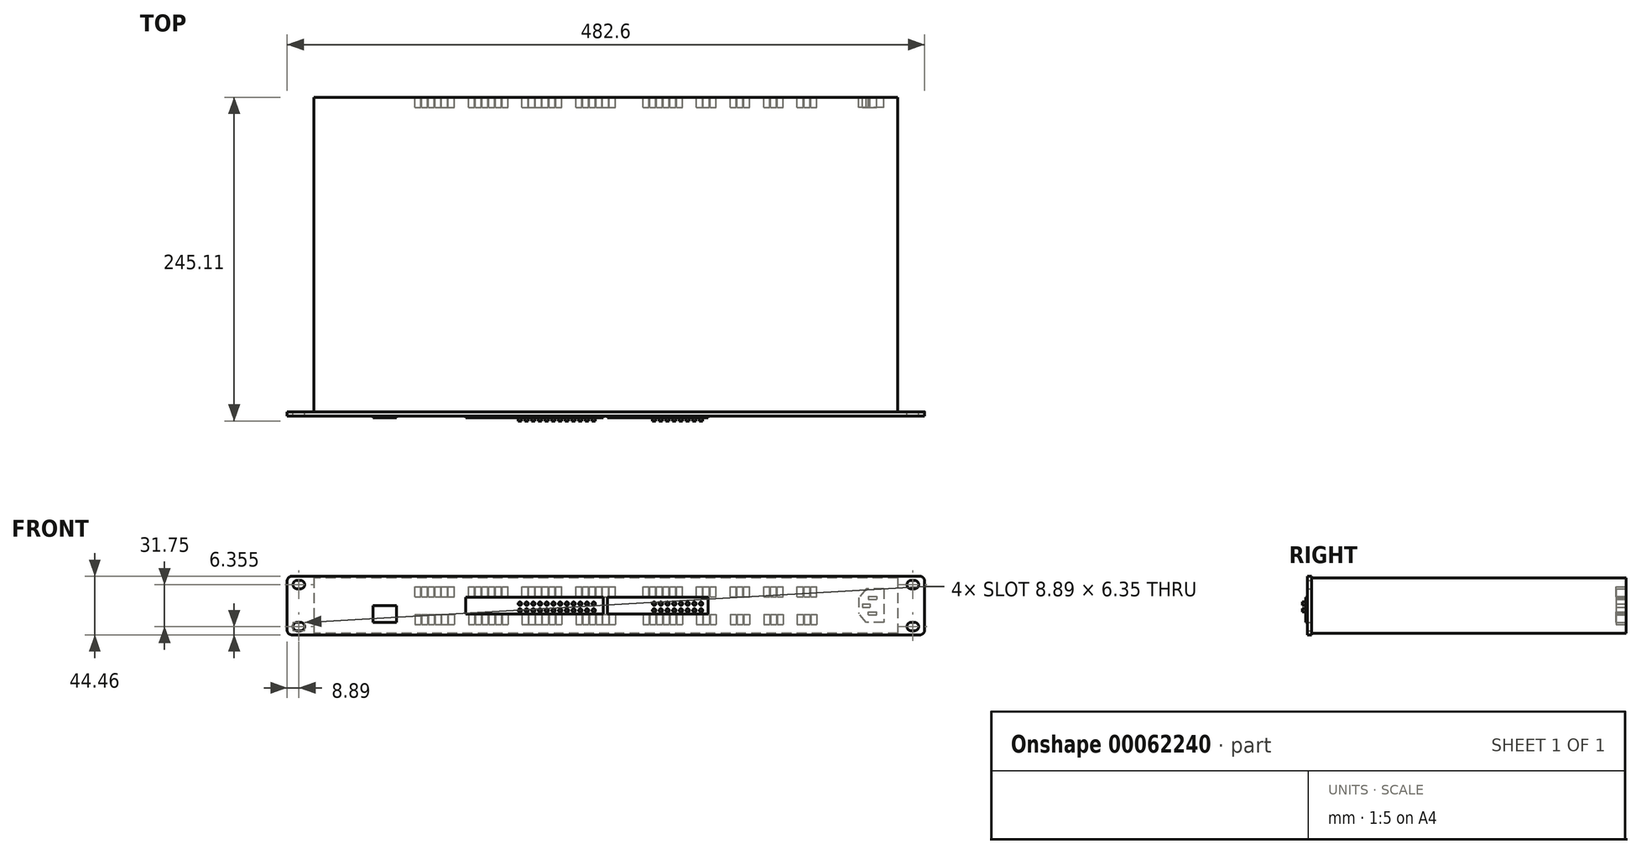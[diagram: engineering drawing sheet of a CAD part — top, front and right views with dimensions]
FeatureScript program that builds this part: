
annotation { "Feature Type Name" : "Feature", "Feature Type Description" : "" }
export const myFeature = defineFeature(function(context is Context, id is Id, definition is map)
    precondition{}
    {
        {
            var Q0;
            Q0=qCreatedBy(makeId("Front.planeOp"),FACE);
            var sketch = newSketch(context, id + "F0", { "sketchPlane" : qUnion([Q0])});
            skLineSegment(sketch, "E0.bottom", {"start": v(-237.5, 22.23) * mm, "end": v(237.5, 22.23) * mm});
            skLineSegment(sketch, "E0.top", {"start": v(-237.5, -22.22) * mm, "end": v(237.5, -22.22) * mm});
            skLineSegment(sketch, "E0.left", {"start": v(-241.3, 18.42) * mm, "end": v(-241.3, -18.41) * mm});
            skLineSegment(sketch, "E0.right", {"start": v(241.3, 18.42) * mm, "end": v(241.3, -18.42) * mm});
            skPoint(sketch, "E0.middle", {"position": v(0, 0) * mm});
            skArc(sketch, "E1", {"start": v(-233.68, 19.05) * mm, "mid": v(-236.86, 15.88) * mm, "end": v(-233.68, 12.7) * mm});
            skArc(sketch, "E2", {"start": v(-231.14, 12.7) * mm, "mid": v(-227.97, 15.88) * mm, "end": v(-231.14, 19.05) * mm});
            skLineSegment(sketch, "E3", {"start": v(-233.68, 12.7) * mm, "end": v(-231.14, 12.7) * mm});
            skLineSegment(sketch, "E4", {"start": v(-233.68, 19.05) * mm, "end": v(-231.14, 19.05) * mm});
            skPoint(sketch, "E5.visualSharp", {"position": v(-241.3, 22.23) * mm});
            skArc(sketch, "E5.filletArc", {"start": v(-237.5, 22.23) * mm, "mid": v(-240.18, 21.1) * mm, "end": v(-241.3, 18.42) * mm});
            skPoint(sketch, "E6.visualSharp", {"position": v(-241.3, -22.22) * mm});
            skArc(sketch, "E6.filletArc", {"start": v(-241.3, -18.41) * mm, "mid": v(-240.18, -21.1) * mm, "end": v(-237.5, -22.22) * mm});
            skPoint(sketch, "E7.visualSharp", {"position": v(241.3, 22.23) * mm});
            skArc(sketch, "E7.filletArc", {"start": v(241.3, 18.42) * mm, "mid": v(240.18, 21.1) * mm, "end": v(237.5, 22.23) * mm});
            skPoint(sketch, "E8.visualSharp", {"position": v(241.3, -22.22) * mm});
            skArc(sketch, "E8.filletArc", {"start": v(237.5, -22.23) * mm, "mid": v(240.18, -21.1) * mm, "end": v(241.3, -18.42) * mm});
            skLineSegment(sketch, "E9.MirrorCS", {"start": v(-233.68, -19.05) * mm, "end": v(-231.14, -19.05) * mm});
            skArc(sketch, "E10.MirrorCS", {"start": v(-231.14, -12.7) * mm, "mid": v(-227.97, -15.88) * mm, "end": v(-231.14, -19.05) * mm});
            skLineSegment(sketch, "E11.MirrorCS", {"start": v(-233.68, -12.7) * mm, "end": v(-231.14, -12.7) * mm});
            skArc(sketch, "E12.MirrorCS", {"start": v(-233.68, -19.05) * mm, "mid": v(-236.86, -15.88) * mm, "end": v(-233.68, -12.7) * mm});
            skLineSegment(sketch, "E13.MirrorCS", {"start": v(233.68, 12.7) * mm, "end": v(231.14, 12.7) * mm});
            skLineSegment(sketch, "E14.MirrorCS", {"start": v(233.68, -12.7) * mm, "end": v(231.14, -12.7) * mm});
            skLineSegment(sketch, "E15.MirrorCS", {"start": v(233.68, 19.05) * mm, "end": v(231.14, 19.05) * mm});
            skLineSegment(sketch, "E16.MirrorCS", {"start": v(233.68, -19.05) * mm, "end": v(231.14, -19.05) * mm});
            skArc(sketch, "E17.MirrorCS", {"start": v(233.68, -19.05) * mm, "mid": v(236.86, -15.88) * mm, "end": v(233.68, -12.7) * mm});
            skArc(sketch, "E18.MirrorCS", {"start": v(231.14, 12.7) * mm, "mid": v(227.97, 15.88) * mm, "end": v(231.14, 19.05) * mm});
            skArc(sketch, "E19.MirrorCS", {"start": v(233.68, 19.05) * mm, "mid": v(236.86, 15.88) * mm, "end": v(233.68, 12.7) * mm});
            skArc(sketch, "E20.MirrorCS", {"start": v(231.14, -12.7) * mm, "mid": v(227.97, -15.88) * mm, "end": v(231.14, -19.05) * mm});
            skSolve(sketch);
        }
        {
            var Q0;
            Q0 = qSketchRegion(id + "F0", true);
            extrude(context, id + "F1", {"entities" : qUnion([Q0]), "depth" : 3.17 * mm});
        }
        {
            var Q0;
            Q0=makeQuery(id+"F1.opExtrude","CAP_FACE",FACE,{"disambiguationData":[OSD([sQuery(id+"F0.wireOp",EDGE,"E0.bottom"),sQuery(id+"F0.wireOp",EDGE,"E0.top"),sQuery(id+"F0.wireOp",EDGE,"E0.left"),sQuery(id+"F0.wireOp",EDGE,"E0.right"),sQuery(id+"F0.wireOp",EDGE,"E1"),sQuery(id+"F0.wireOp",EDGE,"E2"),sQuery(id+"F0.wireOp",EDGE,"E3"),sQuery(id+"F0.wireOp",EDGE,"E4"),sQuery(id+"F0.wireOp",EDGE,"E5.filletArc"),sQuery(id+"F0.wireOp",EDGE,"E6.filletArc"),sQuery(id+"F0.wireOp",EDGE,"E7.filletArc"),sQuery(id+"F0.wireOp",EDGE,"E8.filletArc"),sQuery(id+"F0.wireOp",EDGE,"E9.MirrorCS"),sQuery(id+"F0.wireOp",EDGE,"E10.MirrorCS"),sQuery(id+"F0.wireOp",EDGE,"E11.MirrorCS"),sQuery(id+"F0.wireOp",EDGE,"E12.MirrorCS"),sQuery(id+"F0.wireOp",EDGE,"E13.MirrorCS"),sQuery(id+"F0.wireOp",EDGE,"E14.MirrorCS"),sQuery(id+"F0.wireOp",EDGE,"E15.MirrorCS"),sQuery(id+"F0.wireOp",EDGE,"E16.MirrorCS"),sQuery(id+"F0.wireOp",EDGE,"E17.MirrorCS"),sQuery(id+"F0.wireOp",EDGE,"E18.MirrorCS"),sQuery(id+"F0.wireOp",EDGE,"E19.MirrorCS"),sQuery(id+"F0.wireOp",EDGE,"E20.MirrorCS")])],"isStart":true});
            var sketch = newSketch(context, id + "F2", { "sketchPlane" : qUnion([Q0])});
            skLineSegment(sketch, "E21.bottom", {"start": v(-220.98, 20.96) * mm, "end": v(220.98, 20.96) * mm});
            skLineSegment(sketch, "E21.top", {"start": v(-220.98, -20.95) * mm, "end": v(220.98, -20.95) * mm});
            skLineSegment(sketch, "E21.left", {"start": v(-220.98, 20.96) * mm, "end": v(-220.98, -20.95) * mm});
            skLineSegment(sketch, "E21.right", {"start": v(220.98, 20.96) * mm, "end": v(220.98, -20.95) * mm});
            skPoint(sketch, "E21.middle", {"position": v(0, 0) * mm});
            skSolve(sketch);
        }
        {
            var Q0;
            Q0 = qSketchRegion(id + "F2", true);
            extrude(context, id + "F3", {"entities" : qUnion([Q0]), "operationType" : NewBodyOperationType.ADD, "depth" : 238.12 * mm});
        }
        {
            var Q0;
            Q0=makeQuery(id+"F3.opExtrude","CAP_FACE",FACE,{"disambiguationData":[OSD([sQuery(id+"F2.wireOp",EDGE,"E21.bottom"),sQuery(id+"F2.wireOp",EDGE,"E21.top"),sQuery(id+"F2.wireOp",EDGE,"E21.left"),sQuery(id+"F2.wireOp",EDGE,"E21.right")])],"isStart":false});
            var sketch = newSketch(context, id + "F4", { "sketchPlane" : qUnion([Q0])});
            skLineSegment(sketch, "E22.bottom", {"start": v(-210.48, 12.7) * mm, "end": v(-197.2, 12.7) * mm});
            skLineSegment(sketch, "E22.top", {"start": v(-210.48, -12.7) * mm, "end": v(-197.2, -12.7) * mm});
            skLineSegment(sketch, "E22.left", {"start": v(-210.48, 12.7) * mm, "end": v(-210.48, -12.7) * mm});
            skLineSegment(sketch, "E22.right", {"start": v(-191.43, 6.17) * mm, "end": v(-191.43, -6.17) * mm});
            skPoint(sketch, "E22.middle", {"position": v(-200.95, 0) * mm});
            skLineSegment(sketch, "E23", {"start": v(-197.2, 12.7) * mm, "end": v(-191.43, 6.17) * mm});
            skLineSegment(sketch, "E24", {"start": v(-200.95, 0) * mm, "end": v(229.43, 0) * mm, "construction": true});
            skPoint(sketch, "E24.endSnap0", {"position": v(220.98, 0) * mm});
            skLineSegment(sketch, "E25.MirrorCS", {"start": v(-197.2, -12.7) * mm, "end": v(-191.43, -6.17) * mm});
            skLineSegment(sketch, "E26.bottom", {"start": v(-194.15, 1.21) * mm, "end": v(-199.97, 1.21) * mm});
            skLineSegment(sketch, "E26.top", {"start": v(-194.15, -1.21) * mm, "end": v(-199.97, -1.21) * mm});
            skLineSegment(sketch, "E26.left", {"start": v(-194.15, 1.21) * mm, "end": v(-194.15, -1.21) * mm});
            skLineSegment(sketch, "E26.right", {"start": v(-199.97, 1.21) * mm, "end": v(-199.97, -1.21) * mm});
            skPoint(sketch, "E26.middle", {"position": v(-197.06, 0) * mm});
            skLineSegment(sketch, "E27.bottom", {"start": v(-198.78, 6.9) * mm, "end": v(-205.13, 6.9) * mm});
            skLineSegment(sketch, "E27.top", {"start": v(-198.78, 4.79) * mm, "end": v(-205.13, 4.79) * mm});
            skLineSegment(sketch, "E27.left", {"start": v(-198.78, 6.9) * mm, "end": v(-198.78, 4.79) * mm});
            skLineSegment(sketch, "E27.right", {"start": v(-205.13, 6.9) * mm, "end": v(-205.13, 4.79) * mm});
            skPoint(sketch, "E27.middle", {"position": v(-201.96, 5.84) * mm});
            skPoint(sketch, "E28.MirrorP", {"position": v(-201.96, -5.84) * mm});
            skLineSegment(sketch, "E29.MirrorCS", {"start": v(-198.78, -4.79) * mm, "end": v(-205.13, -4.79) * mm});
            skLineSegment(sketch, "E30.MirrorCS", {"start": v(-198.78, -6.9) * mm, "end": v(-205.13, -6.9) * mm});
            skLineSegment(sketch, "E31.MirrorCS", {"start": v(-198.78, -6.9) * mm, "end": v(-198.78, -4.79) * mm});
            skLineSegment(sketch, "E32.MirrorCS", {"start": v(-205.13, -6.9) * mm, "end": v(-205.13, -4.79) * mm});
            skPoint(sketch, "E33.orphan", {"position": v(-191.43, 12.7) * mm});
            skPoint(sketch, "E34.orphan", {"position": v(-191.43, -12.7) * mm});
            skLineSegment(sketch, "E35.bottom", {"start": v(-155.05, 6.81) * mm, "end": v(-159.62, 6.81) * mm});
            skLineSegment(sketch, "E35.top", {"start": v(-155.05, 14.43) * mm, "end": v(-159.62, 14.43) * mm});
            skLineSegment(sketch, "E35.left", {"start": v(-155.05, 6.81) * mm, "end": v(-155.05, 14.43) * mm});
            skLineSegment(sketch, "E35.right", {"start": v(-159.62, 6.81) * mm, "end": v(-159.62, 14.43) * mm});
            skPoint(sketch, "E35.middle", {"position": v(-157.33, 10.62) * mm});
            skPoint(sketch, "E36.1.0.0", {"position": v(-152.25, 10.62) * mm});
            skLineSegment(sketch, "E36.1.0.1", {"start": v(-149.97, 14.43) * mm, "end": v(-154.54, 14.43) * mm});
            skLineSegment(sketch, "E36.1.0.2", {"start": v(-154.54, 6.81) * mm, "end": v(-154.54, 14.43) * mm});
            skLineSegment(sketch, "E36.1.0.3", {"start": v(-149.97, 6.81) * mm, "end": v(-149.97, 14.43) * mm});
            skLineSegment(sketch, "E36.1.0.4", {"start": v(-149.97, 6.81) * mm, "end": v(-154.54, 6.81) * mm});
            skPoint(sketch, "E36.2.0.0", {"position": v(-147.17, 10.62) * mm});
            skLineSegment(sketch, "E36.2.0.1", {"start": v(-144.89, 14.43) * mm, "end": v(-149.46, 14.43) * mm});
            skLineSegment(sketch, "E36.2.0.2", {"start": v(-149.46, 6.81) * mm, "end": v(-149.46, 14.43) * mm});
            skLineSegment(sketch, "E36.2.0.3", {"start": v(-144.89, 6.81) * mm, "end": v(-144.89, 14.43) * mm});
            skLineSegment(sketch, "E36.2.0.4", {"start": v(-144.89, 6.81) * mm, "end": v(-149.46, 6.81) * mm});
            skPoint(sketch, "E36.3.0.0", {"position": v(-142.1, 10.62) * mm});
            skPoint(sketch, "E36.4.0.0", {"position": v(-137.01, 10.62) * mm});
            skPoint(sketch, "E36.5.0.0", {"position": v(-131.93, 10.62) * mm});
            skLineSegment(sketch, "E36.5.0.1", {"start": v(-129.65, 14.43) * mm, "end": v(-134.22, 14.43) * mm});
            skLineSegment(sketch, "E36.5.0.2", {"start": v(-134.22, 6.81) * mm, "end": v(-134.22, 14.43) * mm});
            skLineSegment(sketch, "E36.5.0.3", {"start": v(-129.65, 6.81) * mm, "end": v(-129.65, 14.43) * mm});
            skLineSegment(sketch, "E36.5.0.4", {"start": v(-129.65, 6.81) * mm, "end": v(-134.22, 6.81) * mm});
            skPoint(sketch, "E36.6.0.0", {"position": v(-126.85, 10.62) * mm});
            skLineSegment(sketch, "E36.6.0.1", {"start": v(-124.57, 14.43) * mm, "end": v(-129.14, 14.43) * mm});
            skLineSegment(sketch, "E36.6.0.2", {"start": v(-129.14, 6.81) * mm, "end": v(-129.14, 14.43) * mm});
            skLineSegment(sketch, "E36.6.0.3", {"start": v(-124.57, 6.81) * mm, "end": v(-124.57, 14.43) * mm});
            skLineSegment(sketch, "E36.6.0.4", {"start": v(-124.57, 6.81) * mm, "end": v(-129.14, 6.81) * mm});
            skPoint(sketch, "E36.7.0.0", {"position": v(-121.77, 10.62) * mm});
            skLineSegment(sketch, "E36.7.0.1", {"start": v(-119.49, 14.43) * mm, "end": v(-124.06, 14.43) * mm});
            skLineSegment(sketch, "E36.7.0.2", {"start": v(-124.06, 6.81) * mm, "end": v(-124.06, 14.43) * mm});
            skLineSegment(sketch, "E36.7.0.3", {"start": v(-119.49, 6.81) * mm, "end": v(-119.49, 14.43) * mm});
            skLineSegment(sketch, "E36.7.0.4", {"start": v(-119.49, 6.81) * mm, "end": v(-124.06, 6.81) * mm});
            skPoint(sketch, "E36.8.0.0", {"position": v(-116.7, 10.62) * mm});
            skPoint(sketch, "E36.9.0.0", {"position": v(-111.61, 10.62) * mm});
            skPoint(sketch, "E36.10.0.0", {"position": v(-106.53, 10.62) * mm});
            skLineSegment(sketch, "E36.10.0.1", {"start": v(-104.25, 14.43) * mm, "end": v(-108.82, 14.43) * mm});
            skLineSegment(sketch, "E36.10.0.2", {"start": v(-108.82, 6.81) * mm, "end": v(-108.82, 14.43) * mm});
            skLineSegment(sketch, "E36.10.0.3", {"start": v(-104.25, 6.81) * mm, "end": v(-104.25, 14.43) * mm});
            skLineSegment(sketch, "E36.10.0.4", {"start": v(-104.25, 6.81) * mm, "end": v(-108.82, 6.81) * mm});
            skPoint(sketch, "E36.11.0.0", {"position": v(-101.45, 10.62) * mm});
            skLineSegment(sketch, "E36.11.0.1", {"start": v(-99.17, 14.43) * mm, "end": v(-103.74, 14.43) * mm});
            skLineSegment(sketch, "E36.11.0.2", {"start": v(-103.74, 6.81) * mm, "end": v(-103.74, 14.43) * mm});
            skLineSegment(sketch, "E36.11.0.3", {"start": v(-99.17, 6.81) * mm, "end": v(-99.17, 14.43) * mm});
            skLineSegment(sketch, "E36.11.0.4", {"start": v(-99.17, 6.81) * mm, "end": v(-103.74, 6.81) * mm});
            skPoint(sketch, "E36.12.0.0", {"position": v(-96.37, 10.62) * mm});
            skLineSegment(sketch, "E36.12.0.1", {"start": v(-94.09, 14.43) * mm, "end": v(-98.66, 14.43) * mm});
            skLineSegment(sketch, "E36.12.0.2", {"start": v(-98.66, 6.81) * mm, "end": v(-98.66, 14.43) * mm});
            skLineSegment(sketch, "E36.12.0.3", {"start": v(-94.09, 6.81) * mm, "end": v(-94.09, 14.43) * mm});
            skLineSegment(sketch, "E36.12.0.4", {"start": v(-94.09, 6.81) * mm, "end": v(-98.66, 6.81) * mm});
            skPoint(sketch, "E36.13.0.0", {"position": v(-91.3, 10.62) * mm});
            skPoint(sketch, "E36.14.0.0", {"position": v(-86.21, 10.62) * mm});
            skPoint(sketch, "E36.15.0.0", {"position": v(-81.13, 10.62) * mm});
            skLineSegment(sketch, "E36.15.0.1", {"start": v(-78.85, 14.43) * mm, "end": v(-83.42, 14.43) * mm});
            skLineSegment(sketch, "E36.15.0.2", {"start": v(-83.42, 6.81) * mm, "end": v(-83.42, 14.43) * mm});
            skLineSegment(sketch, "E36.15.0.3", {"start": v(-78.85, 6.81) * mm, "end": v(-78.85, 14.43) * mm});
            skLineSegment(sketch, "E36.15.0.4", {"start": v(-78.85, 6.81) * mm, "end": v(-83.42, 6.81) * mm});
            skPoint(sketch, "E36.16.0.0", {"position": v(-76.05, 10.62) * mm});
            skLineSegment(sketch, "E36.16.0.1", {"start": v(-73.77, 14.43) * mm, "end": v(-78.34, 14.43) * mm});
            skLineSegment(sketch, "E36.16.0.2", {"start": v(-78.34, 6.81) * mm, "end": v(-78.34, 14.43) * mm});
            skLineSegment(sketch, "E36.16.0.3", {"start": v(-73.77, 6.81) * mm, "end": v(-73.77, 14.43) * mm});
            skLineSegment(sketch, "E36.16.0.4", {"start": v(-73.77, 6.81) * mm, "end": v(-78.34, 6.81) * mm});
            skPoint(sketch, "E36.17.0.0", {"position": v(-70.97, 10.62) * mm});
            skLineSegment(sketch, "E36.17.0.1", {"start": v(-68.69, 14.43) * mm, "end": v(-73.26, 14.43) * mm});
            skLineSegment(sketch, "E36.17.0.2", {"start": v(-73.26, 6.81) * mm, "end": v(-73.26, 14.43) * mm});
            skLineSegment(sketch, "E36.17.0.3", {"start": v(-68.69, 6.81) * mm, "end": v(-68.69, 14.43) * mm});
            skLineSegment(sketch, "E36.17.0.4", {"start": v(-68.69, 6.81) * mm, "end": v(-73.26, 6.81) * mm});
            skPoint(sketch, "E36.18.0.0", {"position": v(-65.9, 10.62) * mm});
            skPoint(sketch, "E36.19.0.0", {"position": v(-60.81, 10.62) * mm});
            skPoint(sketch, "E36.20.0.0", {"position": v(-55.73, 10.62) * mm});
            skLineSegment(sketch, "E36.20.0.1", {"start": v(-53.45, 14.43) * mm, "end": v(-58.02, 14.43) * mm});
            skLineSegment(sketch, "E36.20.0.2", {"start": v(-58.02, 6.81) * mm, "end": v(-58.02, 14.43) * mm});
            skLineSegment(sketch, "E36.20.0.3", {"start": v(-53.45, 6.81) * mm, "end": v(-53.45, 14.43) * mm});
            skLineSegment(sketch, "E36.20.0.4", {"start": v(-53.45, 6.81) * mm, "end": v(-58.02, 6.81) * mm});
            skPoint(sketch, "E36.21.0.0", {"position": v(-50.65, 10.62) * mm});
            skLineSegment(sketch, "E36.21.0.1", {"start": v(-48.37, 14.43) * mm, "end": v(-52.94, 14.43) * mm});
            skLineSegment(sketch, "E36.21.0.2", {"start": v(-52.94, 6.81) * mm, "end": v(-52.94, 14.43) * mm});
            skLineSegment(sketch, "E36.21.0.3", {"start": v(-48.37, 6.81) * mm, "end": v(-48.37, 14.43) * mm});
            skLineSegment(sketch, "E36.21.0.4", {"start": v(-48.37, 6.81) * mm, "end": v(-52.94, 6.81) * mm});
            skPoint(sketch, "E36.22.0.0", {"position": v(-45.57, 10.62) * mm});
            skLineSegment(sketch, "E36.22.0.1", {"start": v(-43.29, 14.43) * mm, "end": v(-47.86, 14.43) * mm});
            skLineSegment(sketch, "E36.22.0.2", {"start": v(-47.86, 6.81) * mm, "end": v(-47.86, 14.43) * mm});
            skLineSegment(sketch, "E36.22.0.3", {"start": v(-43.29, 6.81) * mm, "end": v(-43.29, 14.43) * mm});
            skLineSegment(sketch, "E36.22.0.4", {"start": v(-43.29, 6.81) * mm, "end": v(-47.86, 6.81) * mm});
            skPoint(sketch, "E36.23.0.0", {"position": v(-40.5, 10.62) * mm});
            skLineSegment(sketch, "E36.23.0.1", {"start": v(-38.2, 14.43) * mm, "end": v(-42.78, 14.43) * mm});
            skLineSegment(sketch, "E36.23.0.2", {"start": v(-42.78, 6.81) * mm, "end": v(-42.78, 14.43) * mm});
            skLineSegment(sketch, "E36.23.0.3", {"start": v(-38.2, 6.81) * mm, "end": v(-38.2, 14.43) * mm});
            skLineSegment(sketch, "E36.23.0.4", {"start": v(-38.2, 6.81) * mm, "end": v(-42.78, 6.81) * mm});
            skPoint(sketch, "E36.24.0.0", {"position": v(-35.41, 10.62) * mm});
            skLineSegment(sketch, "E36.24.0.1", {"start": v(-33.13, 14.43) * mm, "end": v(-37.7, 14.43) * mm});
            skLineSegment(sketch, "E36.24.0.2", {"start": v(-37.7, 6.81) * mm, "end": v(-37.7, 14.43) * mm});
            skLineSegment(sketch, "E36.24.0.3", {"start": v(-33.13, 6.81) * mm, "end": v(-33.13, 14.43) * mm});
            skLineSegment(sketch, "E36.24.0.4", {"start": v(-33.13, 6.81) * mm, "end": v(-37.7, 6.81) * mm});
            skPoint(sketch, "E36.25.0.0", {"position": v(-30.33, 10.62) * mm});
            skLineSegment(sketch, "E36.25.0.1", {"start": v(-28.05, 14.43) * mm, "end": v(-32.62, 14.43) * mm});
            skLineSegment(sketch, "E36.25.0.2", {"start": v(-32.62, 6.81) * mm, "end": v(-32.62, 14.43) * mm});
            skLineSegment(sketch, "E36.25.0.3", {"start": v(-28.05, 6.81) * mm, "end": v(-28.05, 14.43) * mm});
            skLineSegment(sketch, "E36.25.0.4", {"start": v(-28.05, 6.81) * mm, "end": v(-32.62, 6.81) * mm});
            skPoint(sketch, "E36.26.0.0", {"position": v(-25.25, 10.62) * mm});
            skPoint(sketch, "E36.27.0.0", {"position": v(-20.17, 10.62) * mm});
            skPoint(sketch, "E36.28.0.0", {"position": v(-15.1, 10.62) * mm});
            skPoint(sketch, "E36.29.0.0", {"position": v(-10.01, 10.62) * mm});
            skPoint(sketch, "E36.30.0.0", {"position": v(-4.93, 10.62) * mm});
            skLineSegment(sketch, "E36.30.0.1", {"start": v(-2.65, 14.43) * mm, "end": v(-7.22, 14.43) * mm});
            skLineSegment(sketch, "E36.30.0.2", {"start": v(-7.22, 6.81) * mm, "end": v(-7.22, 14.43) * mm});
            skLineSegment(sketch, "E36.30.0.3", {"start": v(-2.65, 6.81) * mm, "end": v(-2.65, 14.43) * mm});
            skLineSegment(sketch, "E36.30.0.4", {"start": v(-2.65, 6.81) * mm, "end": v(-7.22, 6.81) * mm});
            skPoint(sketch, "E36.31.0.0", {"position": v(0.15, 10.62) * mm});
            skLineSegment(sketch, "E36.31.0.1", {"start": v(2.43, 14.43) * mm, "end": v(-2.14, 14.43) * mm});
            skLineSegment(sketch, "E36.31.0.2", {"start": v(-2.14, 6.81) * mm, "end": v(-2.14, 14.43) * mm});
            skLineSegment(sketch, "E36.31.0.3", {"start": v(2.43, 6.81) * mm, "end": v(2.43, 14.43) * mm});
            skLineSegment(sketch, "E36.31.0.4", {"start": v(2.43, 6.81) * mm, "end": v(-2.14, 6.81) * mm});
            skPoint(sketch, "E36.32.0.0", {"position": v(5.23, 10.62) * mm});
            skLineSegment(sketch, "E36.32.0.1", {"start": v(7.51, 14.43) * mm, "end": v(2.94, 14.43) * mm});
            skLineSegment(sketch, "E36.32.0.2", {"start": v(2.94, 6.81) * mm, "end": v(2.94, 14.43) * mm});
            skLineSegment(sketch, "E36.32.0.3", {"start": v(7.51, 6.81) * mm, "end": v(7.51, 14.43) * mm});
            skLineSegment(sketch, "E36.32.0.4", {"start": v(7.51, 6.81) * mm, "end": v(2.94, 6.81) * mm});
            skPoint(sketch, "E36.33.0.0", {"position": v(10.3, 10.62) * mm});
            skLineSegment(sketch, "E36.33.0.1", {"start": v(12.6, 14.43) * mm, "end": v(8.02, 14.43) * mm});
            skLineSegment(sketch, "E36.33.0.2", {"start": v(8.02, 6.81) * mm, "end": v(8.02, 14.43) * mm});
            skLineSegment(sketch, "E36.33.0.3", {"start": v(12.6, 6.81) * mm, "end": v(12.6, 14.43) * mm});
            skLineSegment(sketch, "E36.33.0.4", {"start": v(12.6, 6.81) * mm, "end": v(8.02, 6.81) * mm});
            skPoint(sketch, "E36.34.0.0", {"position": v(15.39, 10.62) * mm});
            skLineSegment(sketch, "E36.34.0.1", {"start": v(17.67, 14.43) * mm, "end": v(13.1, 14.43) * mm});
            skLineSegment(sketch, "E36.34.0.2", {"start": v(13.1, 6.81) * mm, "end": v(13.1, 14.43) * mm});
            skLineSegment(sketch, "E36.34.0.3", {"start": v(17.67, 6.81) * mm, "end": v(17.67, 14.43) * mm});
            skLineSegment(sketch, "E36.34.0.4", {"start": v(17.67, 6.81) * mm, "end": v(13.1, 6.81) * mm});
            skPoint(sketch, "E36.35.0.0", {"position": v(20.47, 10.62) * mm});
            skLineSegment(sketch, "E36.35.0.1", {"start": v(22.75, 14.43) * mm, "end": v(18.18, 14.43) * mm});
            skLineSegment(sketch, "E36.35.0.2", {"start": v(18.18, 6.81) * mm, "end": v(18.18, 14.43) * mm});
            skLineSegment(sketch, "E36.35.0.3", {"start": v(22.75, 6.81) * mm, "end": v(22.75, 14.43) * mm});
            skLineSegment(sketch, "E36.35.0.4", {"start": v(22.75, 6.81) * mm, "end": v(18.18, 6.81) * mm});
            skPoint(sketch, "E36.36.0.0", {"position": v(25.55, 10.62) * mm});
            skPoint(sketch, "E36.37.0.0", {"position": v(30.63, 10.62) * mm});
            skPoint(sketch, "E36.38.0.0", {"position": v(35.7, 10.62) * mm});
            skLineSegment(sketch, "E36.38.0.1", {"start": v(38, 14.43) * mm, "end": v(33.42, 14.43) * mm});
            skLineSegment(sketch, "E36.38.0.2", {"start": v(33.42, 6.81) * mm, "end": v(33.42, 14.43) * mm});
            skLineSegment(sketch, "E36.38.0.3", {"start": v(38, 6.81) * mm, "end": v(38, 14.43) * mm});
            skLineSegment(sketch, "E36.38.0.4", {"start": v(38, 6.81) * mm, "end": v(33.42, 6.81) * mm});
            skPoint(sketch, "E36.39.0.0", {"position": v(40.79, 10.62) * mm});
            skLineSegment(sketch, "E36.39.0.1", {"start": v(43.07, 14.43) * mm, "end": v(38.5, 14.43) * mm});
            skLineSegment(sketch, "E36.39.0.2", {"start": v(38.5, 6.81) * mm, "end": v(38.5, 14.43) * mm});
            skLineSegment(sketch, "E36.39.0.3", {"start": v(43.07, 6.81) * mm, "end": v(43.07, 14.43) * mm});
            skLineSegment(sketch, "E36.39.0.4", {"start": v(43.07, 6.81) * mm, "end": v(38.5, 6.81) * mm});
            skPoint(sketch, "E36.40.0.0", {"position": v(45.87, 10.62) * mm});
            skLineSegment(sketch, "E36.40.0.1", {"start": v(48.15, 14.43) * mm, "end": v(43.58, 14.43) * mm});
            skLineSegment(sketch, "E36.40.0.2", {"start": v(43.58, 6.81) * mm, "end": v(43.58, 14.43) * mm});
            skLineSegment(sketch, "E36.40.0.3", {"start": v(48.15, 6.81) * mm, "end": v(48.15, 14.43) * mm});
            skLineSegment(sketch, "E36.40.0.4", {"start": v(48.15, 6.81) * mm, "end": v(43.58, 6.81) * mm});
            skPoint(sketch, "E36.41.0.0", {"position": v(50.95, 10.62) * mm});
            skLineSegment(sketch, "E36.41.0.1", {"start": v(53.23, 14.43) * mm, "end": v(48.66, 14.43) * mm});
            skLineSegment(sketch, "E36.41.0.2", {"start": v(48.66, 6.81) * mm, "end": v(48.66, 14.43) * mm});
            skLineSegment(sketch, "E36.41.0.3", {"start": v(53.23, 6.81) * mm, "end": v(53.23, 14.43) * mm});
            skLineSegment(sketch, "E36.41.0.4", {"start": v(53.23, 6.81) * mm, "end": v(48.66, 6.81) * mm});
            skPoint(sketch, "E36.42.0.0", {"position": v(56.03, 10.62) * mm});
            skLineSegment(sketch, "E36.42.0.1", {"start": v(58.31, 14.43) * mm, "end": v(53.74, 14.43) * mm});
            skLineSegment(sketch, "E36.42.0.2", {"start": v(53.74, 6.81) * mm, "end": v(53.74, 14.43) * mm});
            skLineSegment(sketch, "E36.42.0.3", {"start": v(58.31, 6.81) * mm, "end": v(58.31, 14.43) * mm});
            skLineSegment(sketch, "E36.42.0.4", {"start": v(58.31, 6.81) * mm, "end": v(53.74, 6.81) * mm});
            skPoint(sketch, "E36.43.0.0", {"position": v(61.1, 10.62) * mm});
            skLineSegment(sketch, "E36.43.0.1", {"start": v(63.4, 14.43) * mm, "end": v(58.82, 14.43) * mm});
            skLineSegment(sketch, "E36.43.0.2", {"start": v(58.82, 6.81) * mm, "end": v(58.82, 14.43) * mm});
            skLineSegment(sketch, "E36.43.0.3", {"start": v(63.4, 6.81) * mm, "end": v(63.4, 14.43) * mm});
            skLineSegment(sketch, "E36.43.0.4", {"start": v(63.4, 6.81) * mm, "end": v(58.82, 6.81) * mm});
            skPoint(sketch, "E36.44.0.0", {"position": v(66.19, 10.62) * mm});
            skPoint(sketch, "E36.45.0.0", {"position": v(71.27, 10.62) * mm});
            skPoint(sketch, "E36.46.0.0", {"position": v(76.35, 10.62) * mm});
            skLineSegment(sketch, "E36.46.0.1", {"start": v(78.63, 14.43) * mm, "end": v(74.06, 14.43) * mm});
            skLineSegment(sketch, "E36.46.0.2", {"start": v(74.06, 6.81) * mm, "end": v(74.06, 14.43) * mm});
            skLineSegment(sketch, "E36.46.0.3", {"start": v(78.63, 6.81) * mm, "end": v(78.63, 14.43) * mm});
            skLineSegment(sketch, "E36.46.0.4", {"start": v(78.63, 6.81) * mm, "end": v(74.06, 6.81) * mm});
            skPoint(sketch, "E36.47.0.0", {"position": v(81.43, 10.62) * mm});
            skLineSegment(sketch, "E36.47.0.1", {"start": v(83.71, 14.43) * mm, "end": v(79.14, 14.43) * mm});
            skLineSegment(sketch, "E36.47.0.2", {"start": v(79.14, 6.81) * mm, "end": v(79.14, 14.43) * mm});
            skLineSegment(sketch, "E36.47.0.3", {"start": v(83.71, 6.81) * mm, "end": v(83.71, 14.43) * mm});
            skLineSegment(sketch, "E36.47.0.4", {"start": v(83.71, 6.81) * mm, "end": v(79.14, 6.81) * mm});
            skPoint(sketch, "E36.48.0.0", {"position": v(86.5, 10.62) * mm});
            skLineSegment(sketch, "E36.48.0.1", {"start": v(88.8, 14.43) * mm, "end": v(84.22, 14.43) * mm});
            skLineSegment(sketch, "E36.48.0.2", {"start": v(84.22, 6.81) * mm, "end": v(84.22, 14.43) * mm});
            skLineSegment(sketch, "E36.48.0.3", {"start": v(88.8, 6.81) * mm, "end": v(88.8, 14.43) * mm});
            skLineSegment(sketch, "E36.48.0.4", {"start": v(88.8, 6.81) * mm, "end": v(84.22, 6.81) * mm});
            skPoint(sketch, "E36.49.0.0", {"position": v(91.59, 10.62) * mm});
            skLineSegment(sketch, "E36.49.0.1", {"start": v(93.87, 14.43) * mm, "end": v(89.3, 14.43) * mm});
            skLineSegment(sketch, "E36.49.0.2", {"start": v(89.3, 6.81) * mm, "end": v(89.3, 14.43) * mm});
            skLineSegment(sketch, "E36.49.0.3", {"start": v(93.87, 6.81) * mm, "end": v(93.87, 14.43) * mm});
            skLineSegment(sketch, "E36.49.0.4", {"start": v(93.87, 6.81) * mm, "end": v(89.3, 6.81) * mm});
            skLineSegment(sketch, "E36.direction1", {"start": v(-157.33, 10.62) * mm, "end": v(-152.25, 10.62) * mm, "construction": true});
            skPoint(sketch, "E37.0.50.0", {"position": v(96.67, 10.62) * mm});
            skLineSegment(sketch, "E37.1.50.0", {"start": v(98.95, 14.43) * mm, "end": v(94.38, 14.43) * mm});
            skLineSegment(sketch, "E37.4.50.0", {"start": v(94.38, 6.81) * mm, "end": v(94.38, 14.43) * mm});
            skLineSegment(sketch, "E37.7.50.0", {"start": v(98.95, 6.81) * mm, "end": v(98.95, 14.43) * mm});
            skLineSegment(sketch, "E37.10.50.0", {"start": v(98.95, 6.81) * mm, "end": v(94.38, 6.81) * mm});
            skPoint(sketch, "E37.0.51.0", {"position": v(101.75, 10.62) * mm});
            skLineSegment(sketch, "E37.1.51.0", {"start": v(104.03, 14.43) * mm, "end": v(99.46, 14.43) * mm});
            skLineSegment(sketch, "E37.4.51.0", {"start": v(99.46, 6.81) * mm, "end": v(99.46, 14.43) * mm});
            skLineSegment(sketch, "E37.7.51.0", {"start": v(104.03, 6.81) * mm, "end": v(104.03, 14.43) * mm});
            skLineSegment(sketch, "E37.10.51.0", {"start": v(104.03, 6.81) * mm, "end": v(99.46, 6.81) * mm});
            skPoint(sketch, "E37.0.52.0", {"position": v(106.83, 10.62) * mm});
            skPoint(sketch, "E37.0.53.0", {"position": v(111.9, 10.62) * mm});
            skPoint(sketch, "E37.0.54.0", {"position": v(116.99, 10.62) * mm});
            skLineSegment(sketch, "E37.1.54.0", {"start": v(119.27, 14.43) * mm, "end": v(114.7, 14.43) * mm});
            skLineSegment(sketch, "E37.4.54.0", {"start": v(114.7, 6.81) * mm, "end": v(114.7, 14.43) * mm});
            skLineSegment(sketch, "E37.7.54.0", {"start": v(119.27, 6.81) * mm, "end": v(119.27, 14.43) * mm});
            skLineSegment(sketch, "E37.10.54.0", {"start": v(119.27, 6.81) * mm, "end": v(114.7, 6.81) * mm});
            skPoint(sketch, "E37.0.55.0", {"position": v(122.07, 10.62) * mm});
            skLineSegment(sketch, "E37.1.55.0", {"start": v(124.35, 14.43) * mm, "end": v(119.78, 14.43) * mm});
            skLineSegment(sketch, "E37.4.55.0", {"start": v(119.78, 6.81) * mm, "end": v(119.78, 14.43) * mm});
            skLineSegment(sketch, "E37.7.55.0", {"start": v(124.35, 6.81) * mm, "end": v(124.35, 14.43) * mm});
            skLineSegment(sketch, "E37.10.55.0", {"start": v(124.35, 6.81) * mm, "end": v(119.78, 6.81) * mm});
            skPoint(sketch, "E37.0.56.0", {"position": v(127.15, 10.62) * mm});
            skLineSegment(sketch, "E37.1.56.0", {"start": v(129.43, 14.43) * mm, "end": v(124.86, 14.43) * mm});
            skLineSegment(sketch, "E37.4.56.0", {"start": v(124.86, 6.81) * mm, "end": v(124.86, 14.43) * mm});
            skLineSegment(sketch, "E37.7.56.0", {"start": v(129.43, 6.81) * mm, "end": v(129.43, 14.43) * mm});
            skLineSegment(sketch, "E37.10.56.0", {"start": v(129.43, 6.81) * mm, "end": v(124.86, 6.81) * mm});
            skPoint(sketch, "E37.0.57.0", {"position": v(132.23, 10.62) * mm});
            skLineSegment(sketch, "E37.1.57.0", {"start": v(134.51, 14.43) * mm, "end": v(129.94, 14.43) * mm});
            skLineSegment(sketch, "E37.4.57.0", {"start": v(129.94, 6.81) * mm, "end": v(129.94, 14.43) * mm});
            skLineSegment(sketch, "E37.7.57.0", {"start": v(134.51, 6.81) * mm, "end": v(134.51, 14.43) * mm});
            skLineSegment(sketch, "E37.10.57.0", {"start": v(134.51, 6.81) * mm, "end": v(129.94, 6.81) * mm});
            skPoint(sketch, "E37.0.58.0", {"position": v(137.3, 10.62) * mm});
            skLineSegment(sketch, "E37.1.58.0", {"start": v(139.6, 14.43) * mm, "end": v(135.02, 14.43) * mm});
            skLineSegment(sketch, "E37.4.58.0", {"start": v(135.02, 6.81) * mm, "end": v(135.02, 14.43) * mm});
            skLineSegment(sketch, "E37.7.58.0", {"start": v(139.6, 6.81) * mm, "end": v(139.6, 14.43) * mm});
            skLineSegment(sketch, "E37.10.58.0", {"start": v(139.6, 6.81) * mm, "end": v(135.02, 6.81) * mm});
            skPoint(sketch, "E37.0.59.0", {"position": v(142.39, 10.62) * mm});
            skLineSegment(sketch, "E37.1.59.0", {"start": v(144.67, 14.43) * mm, "end": v(140.1, 14.43) * mm});
            skLineSegment(sketch, "E37.4.59.0", {"start": v(140.1, 6.81) * mm, "end": v(140.1, 14.43) * mm});
            skLineSegment(sketch, "E37.7.59.0", {"start": v(144.67, 6.81) * mm, "end": v(144.67, 14.43) * mm});
            skLineSegment(sketch, "E37.10.59.0", {"start": v(144.67, 6.81) * mm, "end": v(140.1, 6.81) * mm});
            skLineSegment(sketch, "E38.MirrorCS", {"start": v(88.8, -6.81) * mm, "end": v(84.22, -6.81) * mm});
            skLineSegment(sketch, "E39.MirrorCS", {"start": v(83.71, -6.81) * mm, "end": v(79.14, -6.81) * mm});
            skLineSegment(sketch, "E40.MirrorCS", {"start": v(83.71, -6.81) * mm, "end": v(83.71, -14.43) * mm});
            skLineSegment(sketch, "E41.MirrorCS", {"start": v(88.8, -6.81) * mm, "end": v(88.8, -14.43) * mm});
            skLineSegment(sketch, "E42.MirrorCS", {"start": v(12.6, -6.81) * mm, "end": v(12.6, -14.43) * mm});
            skLineSegment(sketch, "E43.MirrorCS", {"start": v(7.51, -6.81) * mm, "end": v(7.51, -14.43) * mm});
            skLineSegment(sketch, "E44.MirrorCS", {"start": v(124.35, -6.81) * mm, "end": v(124.35, -14.43) * mm});
            skLineSegment(sketch, "E45.MirrorCS", {"start": v(-42.78, -6.81) * mm, "end": v(-42.78, -14.43) * mm});
            skLineSegment(sketch, "E46.MirrorCS", {"start": v(129.43, -6.81) * mm, "end": v(124.86, -6.81) * mm});
            skLineSegment(sketch, "E47.MirrorCS", {"start": v(124.35, -6.81) * mm, "end": v(119.78, -6.81) * mm});
            skLineSegment(sketch, "E48.MirrorCS", {"start": v(93.87, -6.81) * mm, "end": v(89.3, -6.81) * mm});
            skLineSegment(sketch, "E49.MirrorCS", {"start": v(17.67, -6.81) * mm, "end": v(13.1, -6.81) * mm});
            skLineSegment(sketch, "E50.MirrorCS", {"start": v(12.6, -6.81) * mm, "end": v(8.02, -6.81) * mm});
            skLineSegment(sketch, "E51.MirrorCS", {"start": v(7.51, -6.81) * mm, "end": v(2.94, -6.81) * mm});
            skLineSegment(sketch, "E52.MirrorCS", {"start": v(2.43, -6.81) * mm, "end": v(-2.14, -6.81) * mm});
            skLineSegment(sketch, "E53.MirrorCS", {"start": v(-2.65, -6.81) * mm, "end": v(-7.22, -6.81) * mm});
            skLineSegment(sketch, "E54.MirrorCS", {"start": v(-73.77, -6.81) * mm, "end": v(-78.34, -6.81) * mm});
            skLineSegment(sketch, "E55.MirrorCS", {"start": v(-78.85, -6.81) * mm, "end": v(-83.42, -6.81) * mm});
            skLineSegment(sketch, "E56.MirrorCS", {"start": v(129.43, -14.43) * mm, "end": v(124.86, -14.43) * mm});
            skLineSegment(sketch, "E57.MirrorCS", {"start": v(124.35, -14.43) * mm, "end": v(119.78, -14.43) * mm});
            skLineSegment(sketch, "E58.MirrorCS", {"start": v(93.87, -14.43) * mm, "end": v(89.3, -14.43) * mm});
            skLineSegment(sketch, "E59.MirrorCS", {"start": v(88.8, -14.43) * mm, "end": v(84.22, -14.43) * mm});
            skLineSegment(sketch, "E60.MirrorCS", {"start": v(83.71, -14.43) * mm, "end": v(79.14, -14.43) * mm});
            skLineSegment(sketch, "E61.MirrorCS", {"start": v(17.67, -14.43) * mm, "end": v(13.1, -14.43) * mm});
            skLineSegment(sketch, "E62.MirrorCS", {"start": v(12.6, -14.43) * mm, "end": v(8.02, -14.43) * mm});
            skLineSegment(sketch, "E63.MirrorCS", {"start": v(7.51, -14.43) * mm, "end": v(2.94, -14.43) * mm});
            skLineSegment(sketch, "E64.MirrorCS", {"start": v(-38.2, -14.43) * mm, "end": v(-42.78, -14.43) * mm});
            skLineSegment(sketch, "E65.MirrorCS", {"start": v(-43.29, -14.43) * mm, "end": v(-47.86, -14.43) * mm});
            skLineSegment(sketch, "E66.MirrorCS", {"start": v(124.86, -6.81) * mm, "end": v(124.86, -14.43) * mm});
            skLineSegment(sketch, "E67.MirrorCS", {"start": v(89.3, -6.81) * mm, "end": v(89.3, -14.43) * mm});
            skLineSegment(sketch, "E68.MirrorCS", {"start": v(84.22, -6.81) * mm, "end": v(84.22, -14.43) * mm});
            skLineSegment(sketch, "E69.MirrorCS", {"start": v(13.1, -6.81) * mm, "end": v(13.1, -14.43) * mm});
            skLineSegment(sketch, "E70.MirrorCS", {"start": v(8.02, -6.81) * mm, "end": v(8.02, -14.43) * mm});
            skLineSegment(sketch, "E71.MirrorCS", {"start": v(-2.14, -6.81) * mm, "end": v(-2.14, -14.43) * mm});
            skLineSegment(sketch, "E72.MirrorCS", {"start": v(-78.85, -6.81) * mm, "end": v(-78.85, -14.43) * mm});
            skLineSegment(sketch, "E73.MirrorCS", {"start": v(139.6, -6.81) * mm, "end": v(139.6, -14.43) * mm});
            skLineSegment(sketch, "E74.MirrorCS", {"start": v(134.51, -6.81) * mm, "end": v(134.51, -14.43) * mm});
            skLineSegment(sketch, "E75.MirrorCS", {"start": v(129.94, -6.81) * mm, "end": v(129.94, -14.43) * mm});
            skLineSegment(sketch, "E76.MirrorCS", {"start": v(58.31, -6.81) * mm, "end": v(58.31, -14.43) * mm});
            skLineSegment(sketch, "E77.MirrorCS", {"start": v(48.66, -6.81) * mm, "end": v(48.66, -14.43) * mm});
            skLineSegment(sketch, "E78.MirrorCS", {"start": v(38, -6.81) * mm, "end": v(38, -14.43) * mm});
            skLineSegment(sketch, "E79.MirrorCS", {"start": v(-33.13, -6.81) * mm, "end": v(-33.13, -14.43) * mm});
            skLineSegment(sketch, "E80.MirrorCS", {"start": v(-38.2, -6.81) * mm, "end": v(-38.2, -14.43) * mm});
            skLineSegment(sketch, "E81.MirrorCS", {"start": v(-53.45, -6.81) * mm, "end": v(-53.45, -14.43) * mm});
            skLineSegment(sketch, "E82.MirrorCS", {"start": v(-103.74, -6.81) * mm, "end": v(-103.74, -14.43) * mm});
            skLineSegment(sketch, "E83.MirrorCS", {"start": v(-129.65, -6.81) * mm, "end": v(-129.65, -14.43) * mm});
            skLineSegment(sketch, "E84.MirrorCS", {"start": v(-157.33, -10.62) * mm, "end": v(-152.25, -10.62) * mm, "construction": true});
            skLineSegment(sketch, "E85.MirrorCS", {"start": v(99.46, -6.81) * mm, "end": v(99.46, -14.43) * mm});
            skLineSegment(sketch, "E86.MirrorCS", {"start": v(93.87, -6.81) * mm, "end": v(93.87, -14.43) * mm});
            skLineSegment(sketch, "E87.MirrorCS", {"start": v(-43.29, -6.81) * mm, "end": v(-43.29, -14.43) * mm});
            skLineSegment(sketch, "E88.MirrorCS", {"start": v(-155.05, -6.81) * mm, "end": v(-155.05, -14.43) * mm});
            skLineSegment(sketch, "E89.MirrorCS", {"start": v(144.67, -6.81) * mm, "end": v(140.1, -6.81) * mm});
            skLineSegment(sketch, "E90.MirrorCS", {"start": v(139.6, -6.81) * mm, "end": v(135.02, -6.81) * mm});
            skLineSegment(sketch, "E91.MirrorCS", {"start": v(134.51, -6.81) * mm, "end": v(129.94, -6.81) * mm});
            skLineSegment(sketch, "E92.MirrorCS", {"start": v(104.03, -6.81) * mm, "end": v(99.46, -6.81) * mm});
            skLineSegment(sketch, "E93.MirrorCS", {"start": v(98.95, -6.81) * mm, "end": v(94.38, -6.81) * mm});
            skLineSegment(sketch, "E94.MirrorCS", {"start": v(63.4, -6.81) * mm, "end": v(58.82, -6.81) * mm});
            skLineSegment(sketch, "E95.MirrorCS", {"start": v(58.31, -6.81) * mm, "end": v(53.74, -6.81) * mm});
            skLineSegment(sketch, "E96.MirrorCS", {"start": v(53.23, -6.81) * mm, "end": v(48.66, -6.81) * mm});
            skLineSegment(sketch, "E97.MirrorCS", {"start": v(48.15, -6.81) * mm, "end": v(43.58, -6.81) * mm});
            skLineSegment(sketch, "E98.MirrorCS", {"start": v(43.07, -6.81) * mm, "end": v(38.5, -6.81) * mm});
            skLineSegment(sketch, "E99.MirrorCS", {"start": v(38, -6.81) * mm, "end": v(33.42, -6.81) * mm});
            skLineSegment(sketch, "E100.MirrorCS", {"start": v(-28.05, -6.81) * mm, "end": v(-32.62, -6.81) * mm});
            skLineSegment(sketch, "E101.MirrorCS", {"start": v(-33.13, -6.81) * mm, "end": v(-37.7, -6.81) * mm});
            skLineSegment(sketch, "E102.MirrorCS", {"start": v(-38.2, -6.81) * mm, "end": v(-42.78, -6.81) * mm});
            skLineSegment(sketch, "E103.MirrorCS", {"start": v(-43.29, -6.81) * mm, "end": v(-47.86, -6.81) * mm});
            skLineSegment(sketch, "E104.MirrorCS", {"start": v(-48.37, -6.81) * mm, "end": v(-52.94, -6.81) * mm});
            skLineSegment(sketch, "E105.MirrorCS", {"start": v(-53.45, -6.81) * mm, "end": v(-58.02, -6.81) * mm});
            skLineSegment(sketch, "E106.MirrorCS", {"start": v(-99.17, -6.81) * mm, "end": v(-103.74, -6.81) * mm});
            skLineSegment(sketch, "E107.MirrorCS", {"start": v(-104.25, -6.81) * mm, "end": v(-108.82, -6.81) * mm});
            skLineSegment(sketch, "E108.MirrorCS", {"start": v(-124.57, -6.81) * mm, "end": v(-129.14, -6.81) * mm});
            skLineSegment(sketch, "E109.MirrorCS", {"start": v(-129.65, -6.81) * mm, "end": v(-134.22, -6.81) * mm});
            skLineSegment(sketch, "E110.MirrorCS", {"start": v(-149.97, -6.81) * mm, "end": v(-154.54, -6.81) * mm});
            skLineSegment(sketch, "E111.MirrorCS", {"start": v(-155.05, -6.81) * mm, "end": v(-159.62, -6.81) * mm});
            skLineSegment(sketch, "E112.MirrorCS", {"start": v(144.67, -14.43) * mm, "end": v(140.1, -14.43) * mm});
            skLineSegment(sketch, "E113.MirrorCS", {"start": v(139.6, -14.43) * mm, "end": v(135.02, -14.43) * mm});
            skLineSegment(sketch, "E114.MirrorCS", {"start": v(134.51, -14.43) * mm, "end": v(129.94, -14.43) * mm});
            skLineSegment(sketch, "E115.MirrorCS", {"start": v(104.03, -14.43) * mm, "end": v(99.46, -14.43) * mm});
            skLineSegment(sketch, "E116.MirrorCS", {"start": v(98.95, -14.43) * mm, "end": v(94.38, -14.43) * mm});
            skLineSegment(sketch, "E117.MirrorCS", {"start": v(63.4, -14.43) * mm, "end": v(58.82, -14.43) * mm});
            skLineSegment(sketch, "E118.MirrorCS", {"start": v(58.31, -14.43) * mm, "end": v(53.74, -14.43) * mm});
            skLineSegment(sketch, "E119.MirrorCS", {"start": v(53.23, -14.43) * mm, "end": v(48.66, -14.43) * mm});
            skLineSegment(sketch, "E120.MirrorCS", {"start": v(48.15, -14.43) * mm, "end": v(43.58, -14.43) * mm});
            skLineSegment(sketch, "E121.MirrorCS", {"start": v(43.07, -14.43) * mm, "end": v(38.5, -14.43) * mm});
            skLineSegment(sketch, "E122.MirrorCS", {"start": v(38, -14.43) * mm, "end": v(33.42, -14.43) * mm});
            skLineSegment(sketch, "E123.MirrorCS", {"start": v(2.43, -14.43) * mm, "end": v(-2.14, -14.43) * mm});
            skLineSegment(sketch, "E124.MirrorCS", {"start": v(-2.65, -14.43) * mm, "end": v(-7.22, -14.43) * mm});
            skLineSegment(sketch, "E125.MirrorCS", {"start": v(-28.05, -14.43) * mm, "end": v(-32.62, -14.43) * mm});
            skLineSegment(sketch, "E126.MirrorCS", {"start": v(-33.13, -14.43) * mm, "end": v(-37.7, -14.43) * mm});
            skLineSegment(sketch, "E127.MirrorCS", {"start": v(-48.37, -14.43) * mm, "end": v(-52.94, -14.43) * mm});
            skLineSegment(sketch, "E128.MirrorCS", {"start": v(-53.45, -14.43) * mm, "end": v(-58.02, -14.43) * mm});
            skLineSegment(sketch, "E129.MirrorCS", {"start": v(-73.77, -14.43) * mm, "end": v(-78.34, -14.43) * mm});
            skLineSegment(sketch, "E130.MirrorCS", {"start": v(-78.85, -14.43) * mm, "end": v(-83.42, -14.43) * mm});
            skLineSegment(sketch, "E131.MirrorCS", {"start": v(-99.17, -14.43) * mm, "end": v(-103.74, -14.43) * mm});
            skLineSegment(sketch, "E132.MirrorCS", {"start": v(-104.25, -14.43) * mm, "end": v(-108.82, -14.43) * mm});
            skLineSegment(sketch, "E133.MirrorCS", {"start": v(-124.57, -14.43) * mm, "end": v(-129.14, -14.43) * mm});
            skLineSegment(sketch, "E134.MirrorCS", {"start": v(-129.65, -14.43) * mm, "end": v(-134.22, -14.43) * mm});
            skLineSegment(sketch, "E135.MirrorCS", {"start": v(-149.97, -14.43) * mm, "end": v(-154.54, -14.43) * mm});
            skLineSegment(sketch, "E136.MirrorCS", {"start": v(-155.05, -14.43) * mm, "end": v(-159.62, -14.43) * mm});
            skLineSegment(sketch, "E137.MirrorCS", {"start": v(140.1, -6.81) * mm, "end": v(140.1, -14.43) * mm});
            skLineSegment(sketch, "E138.MirrorCS", {"start": v(135.02, -6.81) * mm, "end": v(135.02, -14.43) * mm});
            skLineSegment(sketch, "E139.MirrorCS", {"start": v(129.43, -6.81) * mm, "end": v(129.43, -14.43) * mm});
            skLineSegment(sketch, "E140.MirrorCS", {"start": v(98.95, -6.81) * mm, "end": v(98.95, -14.43) * mm});
            skLineSegment(sketch, "E141.MirrorCS", {"start": v(94.38, -6.81) * mm, "end": v(94.38, -14.43) * mm});
            skLineSegment(sketch, "E142.MirrorCS", {"start": v(79.14, -6.81) * mm, "end": v(79.14, -14.43) * mm});
            skLineSegment(sketch, "E143.MirrorCS", {"start": v(58.82, -6.81) * mm, "end": v(58.82, -14.43) * mm});
            skLineSegment(sketch, "E144.MirrorCS", {"start": v(53.74, -6.81) * mm, "end": v(53.74, -14.43) * mm});
            skLineSegment(sketch, "E145.MirrorCS", {"start": v(53.23, -6.81) * mm, "end": v(53.23, -14.43) * mm});
            skLineSegment(sketch, "E146.MirrorCS", {"start": v(48.15, -6.81) * mm, "end": v(48.15, -14.43) * mm});
            skLineSegment(sketch, "E147.MirrorCS", {"start": v(43.58, -6.81) * mm, "end": v(43.58, -14.43) * mm});
            skLineSegment(sketch, "E148.MirrorCS", {"start": v(43.07, -6.81) * mm, "end": v(43.07, -14.43) * mm});
            skLineSegment(sketch, "E149.MirrorCS", {"start": v(38.5, -6.81) * mm, "end": v(38.5, -14.43) * mm});
            skLineSegment(sketch, "E150.MirrorCS", {"start": v(2.94, -6.81) * mm, "end": v(2.94, -14.43) * mm});
            skLineSegment(sketch, "E151.MirrorCS", {"start": v(2.43, -6.81) * mm, "end": v(2.43, -14.43) * mm});
            skLineSegment(sketch, "E152.MirrorCS", {"start": v(-2.65, -6.81) * mm, "end": v(-2.65, -14.43) * mm});
            skLineSegment(sketch, "E153.MirrorCS", {"start": v(-32.62, -6.81) * mm, "end": v(-32.62, -14.43) * mm});
            skLineSegment(sketch, "E154.MirrorCS", {"start": v(-37.7, -6.81) * mm, "end": v(-37.7, -14.43) * mm});
            skLineSegment(sketch, "E155.MirrorCS", {"start": v(-47.86, -6.81) * mm, "end": v(-47.86, -14.43) * mm});
            skLineSegment(sketch, "E156.MirrorCS", {"start": v(-48.37, -6.81) * mm, "end": v(-48.37, -14.43) * mm});
            skLineSegment(sketch, "E157.MirrorCS", {"start": v(-52.94, -6.81) * mm, "end": v(-52.94, -14.43) * mm});
            skLineSegment(sketch, "E158.MirrorCS", {"start": v(-78.34, -6.81) * mm, "end": v(-78.34, -14.43) * mm});
            skLineSegment(sketch, "E159.MirrorCS", {"start": v(-98.66, -6.81) * mm, "end": v(-98.66, -14.43) * mm});
            skLineSegment(sketch, "E160.MirrorCS", {"start": v(-99.17, -6.81) * mm, "end": v(-99.17, -14.43) * mm});
            skLineSegment(sketch, "E161.MirrorCS", {"start": v(-104.25, -6.81) * mm, "end": v(-104.25, -14.43) * mm});
            skLineSegment(sketch, "E162.MirrorCS", {"start": v(-129.14, -6.81) * mm, "end": v(-129.14, -14.43) * mm});
            skLineSegment(sketch, "E163.MirrorCS", {"start": v(-149.46, -6.81) * mm, "end": v(-149.46, -14.43) * mm});
            skLineSegment(sketch, "E164.MirrorCS", {"start": v(-149.97, -6.81) * mm, "end": v(-149.97, -14.43) * mm});
            skLineSegment(sketch, "E165.MirrorCS", {"start": v(-154.54, -6.81) * mm, "end": v(-154.54, -14.43) * mm});
            skLineSegment(sketch, "E166.MirrorCS", {"start": v(119.78, -6.81) * mm, "end": v(119.78, -14.43) * mm});
            skLineSegment(sketch, "E167.MirrorCS", {"start": v(119.27, -6.81) * mm, "end": v(119.27, -14.43) * mm});
            skLineSegment(sketch, "E168.MirrorCS", {"start": v(-124.57, -6.81) * mm, "end": v(-124.57, -14.43) * mm});
            skLineSegment(sketch, "E169.MirrorCS", {"start": v(78.63, -6.81) * mm, "end": v(74.06, -6.81) * mm});
            skLineSegment(sketch, "E170.MirrorCS", {"start": v(22.75, -6.81) * mm, "end": v(18.18, -6.81) * mm});
            skLineSegment(sketch, "E171.MirrorCS", {"start": v(-68.69, -6.81) * mm, "end": v(-73.26, -6.81) * mm});
            skLineSegment(sketch, "E172.MirrorCS", {"start": v(-119.49, -6.81) * mm, "end": v(-124.06, -6.81) * mm});
            skLineSegment(sketch, "E173.MirrorCS", {"start": v(22.75, -14.43) * mm, "end": v(18.18, -14.43) * mm});
            skLineSegment(sketch, "E174.MirrorCS", {"start": v(-68.69, -14.43) * mm, "end": v(-73.26, -14.43) * mm});
            skLineSegment(sketch, "E175.MirrorCS", {"start": v(-119.49, -14.43) * mm, "end": v(-124.06, -14.43) * mm});
            skLineSegment(sketch, "E176.MirrorCS", {"start": v(-144.89, -14.43) * mm, "end": v(-149.46, -14.43) * mm});
            skLineSegment(sketch, "E177.MirrorCS", {"start": v(78.63, -6.81) * mm, "end": v(78.63, -14.43) * mm});
            skLineSegment(sketch, "E178.MirrorCS", {"start": v(18.18, -6.81) * mm, "end": v(18.18, -14.43) * mm});
            skLineSegment(sketch, "E179.MirrorCS", {"start": v(17.67, -6.81) * mm, "end": v(17.67, -14.43) * mm});
            skLineSegment(sketch, "E180.MirrorCS", {"start": v(-73.26, -6.81) * mm, "end": v(-73.26, -14.43) * mm});
            skLineSegment(sketch, "E181.MirrorCS", {"start": v(-73.77, -6.81) * mm, "end": v(-73.77, -14.43) * mm});
            skLineSegment(sketch, "E182.MirrorCS", {"start": v(-124.06, -6.81) * mm, "end": v(-124.06, -14.43) * mm});
            skLineSegment(sketch, "E183.MirrorCS", {"start": v(-159.62, -6.81) * mm, "end": v(-159.62, -14.43) * mm});
            skLineSegment(sketch, "E184.MirrorCS", {"start": v(119.27, -6.81) * mm, "end": v(114.7, -6.81) * mm});
            skLineSegment(sketch, "E185.MirrorCS", {"start": v(-94.09, -6.81) * mm, "end": v(-98.66, -6.81) * mm});
            skLineSegment(sketch, "E186.MirrorCS", {"start": v(-144.89, -6.81) * mm, "end": v(-149.46, -6.81) * mm});
            skLineSegment(sketch, "E187.MirrorCS", {"start": v(-94.09, -14.43) * mm, "end": v(-98.66, -14.43) * mm});
            skLineSegment(sketch, "E188.MirrorCS", {"start": v(104.03, -6.81) * mm, "end": v(104.03, -14.43) * mm});
            skLineSegment(sketch, "E189.MirrorCS", {"start": v(22.75, -6.81) * mm, "end": v(22.75, -14.43) * mm});
            skLineSegment(sketch, "E190.MirrorCS", {"start": v(-68.69, -6.81) * mm, "end": v(-68.69, -14.43) * mm});
            skLineSegment(sketch, "E191.MirrorCS", {"start": v(-144.89, -6.81) * mm, "end": v(-144.89, -14.43) * mm});
            skLineSegment(sketch, "E192.MirrorCS", {"start": v(-134.22, -6.81) * mm, "end": v(-134.22, -14.43) * mm});
            skLineSegment(sketch, "E193.MirrorCS", {"start": v(78.63, -14.43) * mm, "end": v(74.06, -14.43) * mm});
            skLineSegment(sketch, "E194.MirrorCS", {"start": v(-7.22, -6.81) * mm, "end": v(-7.22, -14.43) * mm});
            skLineSegment(sketch, "E195.MirrorCS", {"start": v(-108.82, -6.81) * mm, "end": v(-108.82, -14.43) * mm});
            skLineSegment(sketch, "E196.MirrorCS", {"start": v(74.06, -6.81) * mm, "end": v(74.06, -14.43) * mm});
            skLineSegment(sketch, "E197.MirrorCS", {"start": v(144.67, -6.81) * mm, "end": v(144.67, -14.43) * mm});
            skLineSegment(sketch, "E198.MirrorCS", {"start": v(-28.05, -6.81) * mm, "end": v(-28.05, -14.43) * mm});
            skLineSegment(sketch, "E199.MirrorCS", {"start": v(63.4, -6.81) * mm, "end": v(63.4, -14.43) * mm});
            skLineSegment(sketch, "E200.MirrorCS", {"start": v(-119.49, -6.81) * mm, "end": v(-119.49, -14.43) * mm});
            skLineSegment(sketch, "E201.MirrorCS", {"start": v(-83.42, -6.81) * mm, "end": v(-83.42, -14.43) * mm});
            skLineSegment(sketch, "E202.MirrorCS", {"start": v(114.7, -6.81) * mm, "end": v(114.7, -14.43) * mm});
            skLineSegment(sketch, "E203.MirrorCS", {"start": v(-94.09, -6.81) * mm, "end": v(-94.09, -14.43) * mm});
            skLineSegment(sketch, "E204.MirrorCS", {"start": v(33.42, -6.81) * mm, "end": v(33.42, -14.43) * mm});
            skLineSegment(sketch, "E205.MirrorCS", {"start": v(119.27, -14.43) * mm, "end": v(114.7, -14.43) * mm});
            skLineSegment(sketch, "E206.MirrorCS", {"start": v(-58.02, -6.81) * mm, "end": v(-58.02, -14.43) * mm});
            skPoint(sketch, "E207.MirrorP", {"position": v(-76.05, -10.62) * mm});
            skPoint(sketch, "E208.MirrorP", {"position": v(76.35, -10.62) * mm});
            skPoint(sketch, "E209.MirrorP", {"position": v(-86.21, -10.62) * mm});
            skPoint(sketch, "E210.MirrorP", {"position": v(-4.93, -10.62) * mm});
            skPoint(sketch, "E211.MirrorP", {"position": v(86.5, -10.62) * mm});
            skPoint(sketch, "E212.MirrorP", {"position": v(5.23, -10.62) * mm});
            skPoint(sketch, "E213.MirrorP", {"position": v(101.75, -10.62) * mm});
            skPoint(sketch, "E214.MirrorP", {"position": v(96.67, -10.62) * mm});
            skPoint(sketch, "E215.MirrorP", {"position": v(20.47, -10.62) * mm});
            skPoint(sketch, "E216.MirrorP", {"position": v(15.39, -10.62) * mm});
            skPoint(sketch, "E217.MirrorP", {"position": v(-60.81, -10.62) * mm});
            skPoint(sketch, "E218.MirrorP", {"position": v(-65.9, -10.62) * mm});
            skPoint(sketch, "E219.MirrorP", {"position": v(-70.97, -10.62) * mm});
            skPoint(sketch, "E220.MirrorP", {"position": v(-142.1, -10.62) * mm});
            skPoint(sketch, "E221.MirrorP", {"position": v(-147.17, -10.62) * mm});
            skPoint(sketch, "E222.MirrorP", {"position": v(-152.25, -10.62) * mm});
            skPoint(sketch, "E223.MirrorP", {"position": v(-157.33, -10.62) * mm});
            skPoint(sketch, "E224.MirrorP", {"position": v(66.19, -10.62) * mm});
            skPoint(sketch, "E225.MirrorP", {"position": v(0.15, -10.62) * mm});
            skPoint(sketch, "E226.MirrorP", {"position": v(10.3, -10.62) * mm});
            skPoint(sketch, "E227.MirrorP", {"position": v(-96.37, -10.62) * mm});
            skPoint(sketch, "E228.MirrorP", {"position": v(-10.01, -10.62) * mm});
            skPoint(sketch, "E229.MirrorP", {"position": v(-91.3, -10.62) * mm});
            skPoint(sketch, "E230.MirrorP", {"position": v(91.59, -10.62) * mm});
            skPoint(sketch, "E231.MirrorP", {"position": v(81.43, -10.62) * mm});
            skPoint(sketch, "E232.MirrorP", {"position": v(-81.13, -10.62) * mm});
            skPoint(sketch, "E233.MirrorP", {"position": v(71.27, -10.62) * mm});
            skPoint(sketch, "E234.MirrorP", {"position": v(-15.1, -10.62) * mm});
            skPoint(sketch, "E235.MirrorP", {"position": v(61.1, -10.62) * mm});
            skPoint(sketch, "E236.MirrorP", {"position": v(142.39, -10.62) * mm});
            skPoint(sketch, "E237.MirrorP", {"position": v(-101.45, -10.62) * mm});
            skPoint(sketch, "E238.MirrorP", {"position": v(-20.17, -10.62) * mm});
            skPoint(sketch, "E239.MirrorP", {"position": v(56.03, -10.62) * mm});
            skPoint(sketch, "E240.MirrorP", {"position": v(137.3, -10.62) * mm});
            skPoint(sketch, "E241.MirrorP", {"position": v(-25.25, -10.62) * mm});
            skPoint(sketch, "E242.MirrorP", {"position": v(-106.53, -10.62) * mm});
            skPoint(sketch, "E243.MirrorP", {"position": v(50.95, -10.62) * mm});
            skPoint(sketch, "E244.MirrorP", {"position": v(132.23, -10.62) * mm});
            skPoint(sketch, "E245.MirrorP", {"position": v(-111.61, -10.62) * mm});
            skPoint(sketch, "E246.MirrorP", {"position": v(-30.33, -10.62) * mm});
            skPoint(sketch, "E247.MirrorP", {"position": v(45.87, -10.62) * mm});
            skPoint(sketch, "E248.MirrorP", {"position": v(127.15, -10.62) * mm});
            skPoint(sketch, "E249.MirrorP", {"position": v(-116.7, -10.62) * mm});
            skPoint(sketch, "E250.MirrorP", {"position": v(-35.41, -10.62) * mm});
            skPoint(sketch, "E251.MirrorP", {"position": v(40.79, -10.62) * mm});
            skPoint(sketch, "E252.MirrorP", {"position": v(122.07, -10.62) * mm});
            skPoint(sketch, "E253.MirrorP", {"position": v(-40.5, -10.62) * mm});
            skPoint(sketch, "E254.MirrorP", {"position": v(-121.77, -10.62) * mm});
            skPoint(sketch, "E255.MirrorP", {"position": v(35.7, -10.62) * mm});
            skPoint(sketch, "E256.MirrorP", {"position": v(116.99, -10.62) * mm});
            skPoint(sketch, "E257.MirrorP", {"position": v(-45.57, -10.62) * mm});
            skPoint(sketch, "E258.MirrorP", {"position": v(-126.85, -10.62) * mm});
            skPoint(sketch, "E259.MirrorP", {"position": v(30.63, -10.62) * mm});
            skPoint(sketch, "E260.MirrorP", {"position": v(111.9, -10.62) * mm});
            skPoint(sketch, "E261.MirrorP", {"position": v(-131.93, -10.62) * mm});
            skPoint(sketch, "E262.MirrorP", {"position": v(-50.65, -10.62) * mm});
            skPoint(sketch, "E263.MirrorP", {"position": v(25.55, -10.62) * mm});
            skPoint(sketch, "E264.MirrorP", {"position": v(106.83, -10.62) * mm});
            skPoint(sketch, "E265.MirrorP", {"position": v(-137.01, -10.62) * mm});
            skPoint(sketch, "E266.MirrorP", {"position": v(-55.73, -10.62) * mm});
            skSolve(sketch);
        }
        {
            var Q0;
            Q0 = qSketchRegion(id + "F4", true);
            extrude(context, id + "F5", {"entities" : qUnion([Q0]), "operationType" : NewBodyOperationType.REMOVE, "oppositeDirection" : true, "depth" : 7.62 * mm});
        }
        {
            var Q0;
            Q0=makeQuery(id+"F1.opExtrude","CAP_FACE",FACE,{"disambiguationData":[OSD([sQuery(id+"F0.wireOp",EDGE,"E0.bottom"),sQuery(id+"F0.wireOp",EDGE,"E0.top"),sQuery(id+"F0.wireOp",EDGE,"E0.left"),sQuery(id+"F0.wireOp",EDGE,"E0.right"),sQuery(id+"F0.wireOp",EDGE,"E1"),sQuery(id+"F0.wireOp",EDGE,"E2"),sQuery(id+"F0.wireOp",EDGE,"E3"),sQuery(id+"F0.wireOp",EDGE,"E4"),sQuery(id+"F0.wireOp",EDGE,"E5.filletArc"),sQuery(id+"F0.wireOp",EDGE,"E6.filletArc"),sQuery(id+"F0.wireOp",EDGE,"E7.filletArc"),sQuery(id+"F0.wireOp",EDGE,"E8.filletArc"),sQuery(id+"F0.wireOp",EDGE,"E9.MirrorCS"),sQuery(id+"F0.wireOp",EDGE,"E10.MirrorCS"),sQuery(id+"F0.wireOp",EDGE,"E11.MirrorCS"),sQuery(id+"F0.wireOp",EDGE,"E12.MirrorCS"),sQuery(id+"F0.wireOp",EDGE,"E13.MirrorCS"),sQuery(id+"F0.wireOp",EDGE,"E14.MirrorCS"),sQuery(id+"F0.wireOp",EDGE,"E15.MirrorCS"),sQuery(id+"F0.wireOp",EDGE,"E16.MirrorCS"),sQuery(id+"F0.wireOp",EDGE,"E17.MirrorCS"),sQuery(id+"F0.wireOp",EDGE,"E18.MirrorCS"),sQuery(id+"F0.wireOp",EDGE,"E19.MirrorCS"),sQuery(id+"F0.wireOp",EDGE,"E20.MirrorCS")])],"isStart":false});
            var sketch = newSketch(context, id + "F6", { "sketchPlane" : qUnion([Q0])});
            skLineSegment(sketch, "E267.bottom", {"start": v(-105.96, 6.35) * mm, "end": v(-1.82, 6.35) * mm});
            skLineSegment(sketch, "E267.top", {"start": v(-105.96, -6.35) * mm, "end": v(-1.82, -6.35) * mm});
            skLineSegment(sketch, "E267.left", {"start": v(-105.96, 6.35) * mm, "end": v(-105.96, -6.35) * mm});
            skLineSegment(sketch, "E267.right", {"start": v(-1.82, 6.35) * mm, "end": v(-1.82, -6.35) * mm});
            skPoint(sketch, "E267.middle", {"position": v(-53.89, 0) * mm});
            skLineSegment(sketch, "E268.bottom", {"start": v(77.4, 6.35) * mm, "end": v(1.2, 6.35) * mm});
            skLineSegment(sketch, "E268.top", {"start": v(77.4, -6.35) * mm, "end": v(1.2, -6.35) * mm});
            skLineSegment(sketch, "E268.left", {"start": v(77.4, 6.35) * mm, "end": v(77.4, -6.35) * mm});
            skLineSegment(sketch, "E268.right", {"start": v(1.2, 6.35) * mm, "end": v(1.2, -6.35) * mm});
            skPoint(sketch, "E268.middle", {"position": v(39.3, 0) * mm});
            skLineSegment(sketch, "E269.bottom", {"start": v(-176.33, 0) * mm, "end": v(-158.55, 0) * mm});
            skLineSegment(sketch, "E269.top", {"start": v(-176.33, -12.7) * mm, "end": v(-158.55, -12.7) * mm});
            skLineSegment(sketch, "E269.left", {"start": v(-176.33, 0) * mm, "end": v(-176.33, -12.7) * mm});
            skLineSegment(sketch, "E269.right", {"start": v(-158.55, 0) * mm, "end": v(-158.55, -12.7) * mm});
            skSolve(sketch);
        }
        {
            var Q0;
            Q0=makeQuery(id+"F6.imprint","IMPRINT",FACE,{"disambiguationData":[TD([[makeQuery(id+"F6.imprint","IMPRINT",EDGE,{"derivedFrom":sQuery(id+"F6.wireOp",EDGE,"E267.bottom")}),-1.0]])]});
            var Q1;
            Q1=makeQuery(id+"F6.imprint","IMPRINT",FACE,{"disambiguationData":[TD([[makeQuery(id+"F6.imprint","IMPRINT",EDGE,{"derivedFrom":sQuery(id+"F6.wireOp",EDGE,"E268.bottom")}),1.0]])]});
            var Q2;
            Q2=makeQuery(id+"F6.imprint","IMPRINT",FACE,{"disambiguationData":[TD([[makeQuery(id+"F6.imprint","IMPRINT",EDGE,{"derivedFrom":sQuery(id+"F6.wireOp",EDGE,"E269.bottom")}),-1.0]])]});
            extrude(context, id + "F7", {"entities" : qUnion([Q0, Q1, Q2]), "operationType" : NewBodyOperationType.ADD, "depth" : 1.27 * mm});
        }
        {
            var Q0;
            Q0=makeQuery(id+"F7.opExtrude","CAP_FACE",FACE,{"disambiguationData":[OSD([sQuery(id+"F6.wireOp",EDGE,"E267.bottom"),sQuery(id+"F6.wireOp",EDGE,"E267.top"),sQuery(id+"F6.wireOp",EDGE,"E267.left"),sQuery(id+"F6.wireOp",EDGE,"E267.right")])],"isStart":false});
            var sketch = newSketch(context, id + "F8", { "sketchPlane" : qUnion([Q0])});
            skCircle(sketch, "E270.3.0.0", {"center": v(-65.04, 1.45) * mm, "radius": 1.27 * mm});
            skCircle(sketch, "E270.3.1.0", {"center": v(-65.04, -3.63) * mm, "radius": 1.27 * mm});
            skCircle(sketch, "E270.4.0.0", {"center": v(-59.96, 1.45) * mm, "radius": 1.27 * mm});
            skCircle(sketch, "E270.4.1.0", {"center": v(-59.96, -3.63) * mm, "radius": 1.27 * mm});
            skCircle(sketch, "E270.5.0.0", {"center": v(-54.88, 1.45) * mm, "radius": 1.27 * mm});
            skCircle(sketch, "E270.5.1.0", {"center": v(-54.88, -3.63) * mm, "radius": 1.27 * mm});
            skCircle(sketch, "E270.6.0.0", {"center": v(-49.8, 1.45) * mm, "radius": 1.27 * mm});
            skCircle(sketch, "E270.6.1.0", {"center": v(-49.8, -3.63) * mm, "radius": 1.27 * mm});
            skCircle(sketch, "E270.7.0.0", {"center": v(-44.72, 1.45) * mm, "radius": 1.27 * mm});
            skCircle(sketch, "E270.7.1.0", {"center": v(-44.72, -3.63) * mm, "radius": 1.27 * mm});
            skCircle(sketch, "E270.8.0.0", {"center": v(-39.64, 1.45) * mm, "radius": 1.27 * mm});
            skCircle(sketch, "E270.8.1.0", {"center": v(-39.64, -3.63) * mm, "radius": 1.27 * mm});
            skCircle(sketch, "E270.9.0.0", {"center": v(-34.56, 1.45) * mm, "radius": 1.27 * mm});
            skCircle(sketch, "E270.9.1.0", {"center": v(-34.56, -3.63) * mm, "radius": 1.27 * mm});
            skCircle(sketch, "E270.10.0.0", {"center": v(-29.48, 1.45) * mm, "radius": 1.27 * mm});
            skCircle(sketch, "E270.10.1.0", {"center": v(-29.48, -3.63) * mm, "radius": 1.27 * mm});
            skCircle(sketch, "E270.11.0.0", {"center": v(-24.4, 1.45) * mm, "radius": 1.27 * mm});
            skCircle(sketch, "E270.11.1.0", {"center": v(-24.4, -3.63) * mm, "radius": 1.27 * mm});
            skCircle(sketch, "E270.12.0.0", {"center": v(-19.32, 1.45) * mm, "radius": 1.27 * mm});
            skCircle(sketch, "E270.12.1.0", {"center": v(-19.32, -3.63) * mm, "radius": 1.27 * mm});
            skCircle(sketch, "E270.13.0.0", {"center": v(-14.24, 1.45) * mm, "radius": 1.27 * mm});
            skCircle(sketch, "E270.13.1.0", {"center": v(-14.24, -3.63) * mm, "radius": 1.27 * mm});
            skCircle(sketch, "E270.14.0.0", {"center": v(-9.16, 1.45) * mm, "radius": 1.27 * mm});
            skCircle(sketch, "E270.14.1.0", {"center": v(-9.16, -3.63) * mm, "radius": 1.27 * mm});
            skCircle(sketch, "E270.23.0.0", {"center": v(36.56, 1.45) * mm, "radius": 1.27 * mm});
            skCircle(sketch, "E270.23.1.0", {"center": v(36.56, -3.63) * mm, "radius": 1.27 * mm});
            skCircle(sketch, "E270.24.0.0", {"center": v(41.64, 1.45) * mm, "radius": 1.27 * mm});
            skCircle(sketch, "E270.24.1.0", {"center": v(41.64, -3.63) * mm, "radius": 1.27 * mm});
            skCircle(sketch, "E270.25.0.0", {"center": v(46.72, 1.45) * mm, "radius": 1.27 * mm});
            skCircle(sketch, "E270.25.1.0", {"center": v(46.72, -3.63) * mm, "radius": 1.27 * mm});
            skCircle(sketch, "E270.26.0.0", {"center": v(51.8, 1.45) * mm, "radius": 1.27 * mm});
            skCircle(sketch, "E270.26.1.0", {"center": v(51.8, -3.63) * mm, "radius": 1.27 * mm});
            skCircle(sketch, "E270.27.0.0", {"center": v(56.88, 1.45) * mm, "radius": 1.27 * mm});
            skCircle(sketch, "E270.27.1.0", {"center": v(56.88, -3.63) * mm, "radius": 1.27 * mm});
            skCircle(sketch, "E270.28.0.0", {"center": v(61.96, 1.45) * mm, "radius": 1.27 * mm});
            skCircle(sketch, "E270.28.1.0", {"center": v(61.96, -3.63) * mm, "radius": 1.27 * mm});
            skCircle(sketch, "E270.29.0.0", {"center": v(67.04, 1.45) * mm, "radius": 1.27 * mm});
            skCircle(sketch, "E270.29.1.0", {"center": v(67.04, -3.63) * mm, "radius": 1.27 * mm});
            skCircle(sketch, "E270.30.0.0", {"center": v(72.12, 1.45) * mm, "radius": 1.27 * mm});
            skCircle(sketch, "E270.30.1.0", {"center": v(72.12, -3.63) * mm, "radius": 1.27 * mm});
            skLineSegment(sketch, "E270.direction1", {"start": v(-80.28, 1.45) * mm, "end": v(-75.2, 1.45) * mm, "construction": true});
            skLineSegment(sketch, "E270.direction2", {"start": v(-80.28, 1.45) * mm, "end": v(-80.28, -3.63) * mm, "construction": true});
            skSolve(sketch);
        }
        {
            var Q0;
            Q0 = qSketchRegion(id + "F8", true);
            extrude(context, id + "F9", {"entities" : qUnion([Q0]), "operationType" : NewBodyOperationType.ADD, "depth" : 2.54 * mm});
        }
    });
